# Revit family: Access_Door-General_Purpose-Cendrex-All_Surface_Types-AHD
name_source: partatom
category: Specialty Equipment
revit_build: Autodesk Revit Architecture 2013 (Build: 20130531_2115(x64)
units: mm (PartAtom-declared; Revit-internal decimal feet)

## types (23) — shared parameters
Assembly Code = C1020700
Available Options = http://cendrex.com
Cendrex LEED Ready Program = http://www.cendrex.com
Construction Material = Metal - Cendrex - Aluminum
Default Elevation = 0"
Description = General purpose access door for all surface types
Finish = Metal - Cendrex - Powder Coated White
Frame Depth = 1 7/16"
Manufacturer = Cendrex
Max Area = 1296 in²
Model = AHD
Neoprene Gasket Material = Neoprene - Cendrex -  Gasket
Product Documentation Link = http://cendrex.com
Product Page URL = http://cendrex.com
URL = http://www.cendrex.com

## per-type parameters (varying)
| type | Actual Area | Door Height | Door Width | Height Actual | Height Calc | Width Actual | Width Calc |
| 6 x 6 | 36 in² | 6" | 6" | 8 1/4" | 6" | 8 1/4" | 6" |
| 8 x 8 | 64 in² | 8" | 8" | 10 1/4" | 8" | 10 1/4" | 8" |
| 8 x 12 | 96 in² | 12" | 8" | 14 1/4" | 12" | 10 1/4" | 8" |
| 10 x 10 | 100 in² | 10" | 10" | 12 1/4" | 10" | 12 1/4" | 10" |
| 12 x 12 | 144 in² | 12" | 12" | 14 1/4" | 12" | 14 1/4" | 12" |
| 14 x 14 | 196 in² | 14" | 14" | 16 1/4" | 14" | 16 1/4" | 14" |
| 12 x 16 | 192 in² | 16" | 12" | 18 1/4" | 16" | 14 1/4" | 12" |
| 12 x 18 | 216 in² | 18" | 12" | 20 1/4" | 18" | 14 1/4" | 12" |
| 12 x 24 | 288 in² | 24" | 12" | 26 1/4" | 24" | 14 1/4" | 12" |
| 16 x 16 | 256 in² | 16" | 16" | 18 1/4" | 16" | 18 1/4" | 16" |
| 18 x 18 | 324 in² | 18" | 18" | 20 1/4" | 18" | 20 1/4" | 18" |
| 18 x 24 | 432 in² | 24" | 18" | 26 1/4" | 24" | 20 1/4" | 18" |
| 20 x 20 | 400 in² | 20" | 20" | 22 1/4" | 20" | 22 1/4" | 20" |
| 22 x 22 | 484 in² | 22" | 22" | 24 1/4" | 22" | 24 1/4" | 22" |
| 22 x 30 | 660 in² | 30" | 22" | 32 1/4" | 30" | 24 1/4" | 22" |
| 22 x 36 | 792 in² | 36" | 22" | 38 1/4" | 36" | 24 1/4" | 22" |
| 24 x 24 | 576 in² | 24" | 24" | 26 1/4" | 24" | 26 1/4" | 24" |
| 24 x 30 | 720 in² | 30" | 24" | 32 1/4" | 30" | 26 1/4" | 24" |
| 24 x 36 | 864 in² | 36" | 24" | 38 1/4" | 36" | 26 1/4" | 24" |
| 24 x 48 | 1152 in² | 48" | 24" | 50 1/4" | 48" | 26 1/4" | 24" |
| 30 x 30 | 900 in² | 30" | 30" | 32 1/4" | 30" | 32 1/4" | 30" |
| 36 x 36 | 1296 in² | 36" | 36" | 38 1/4" | 36" | 38 1/4" | 36" |
| Custom | 576 in² | 24" | 24" | 26 1/4" | 24" | 26 1/4" | 24" |

## geometry (parser evidence)
native form markers: Blend x24, Sweep x10
no freeform markers — native parametric forms only
